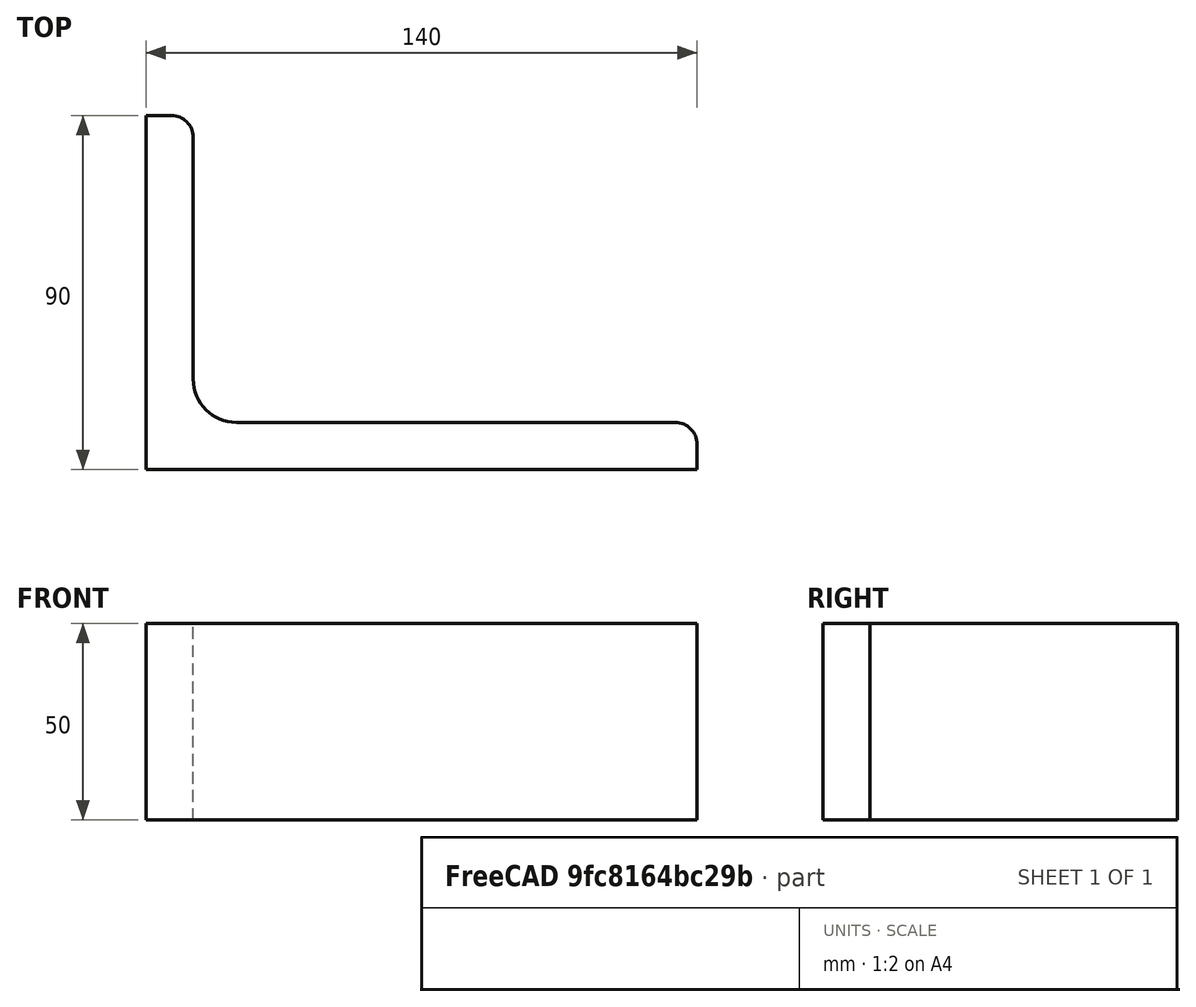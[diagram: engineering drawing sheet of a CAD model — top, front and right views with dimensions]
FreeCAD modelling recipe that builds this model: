
FCSTD DOCUMENT  (FreeCAD 0.15R4671 (Git))
Label: Angle Bar 140x90x12 EN10056 S235JR
License: All rights reserved
LicenseURL: http://en.wikipedia.org/wiki/All_rights_reserved
objects: Sketcher::SketchObject×1, Part::Extrusion×1
note: 2 computed .brp shape members not serialized (recipe doc carries the construction recipe); baked Part::Feature solids carry a one-line shape summary decoded from their .brp

FEATURE [Sketcher::SketchObject] Sketch
  sketch-geometry (9):
    g0: LineSegment StartX=0 StartY=0 StartZ=0 EndX=140 EndY=0 EndZ=0
    g1: LineSegment StartX=140 StartY=0 StartZ=0 EndX=140 EndY=6.5 EndZ=0
    g2: LineSegment StartX=134.5 StartY=12 StartZ=0 EndX=23 EndY=12 EndZ=0
    g3: LineSegment StartX=0 StartY=0 StartZ=0 EndX=0 EndY=90 EndZ=0
    g4: LineSegment StartX=0 StartY=90 StartZ=0 EndX=6.5 EndY=90 EndZ=0
    g5: LineSegment StartX=12 StartY=84.5 StartZ=0 EndX=12 EndY=23 EndZ=0
    g6: ArcOfCircle CenterX=23 CenterY=23 CenterZ=0 NormalX=0 NormalY=0 NormalZ=1 Radius=11 StartAngle=3.14159 EndAngle=4.71239
    g7: ArcOfCircle CenterX=6.5 CenterY=84.5 CenterZ=0 NormalX=0 NormalY=0 NormalZ=1 Radius=5.5 StartAngle=0 EndAngle=1.5708
    g8: ArcOfCircle CenterX=134.5 CenterY=6.5 CenterZ=0 NormalX=0 NormalY=0 NormalZ=1 Radius=5.5 StartAngle=0 EndAngle=1.5708
  constraints (23):
    c: Coincident(g0,g-1)
    c: Horizontal(g0)
    c: Coincident(g1,g0)
    c: Vertical(g1)
    c: Horizontal(g2)
    c: Coincident(g3,g-1)
    c: Vertical(g3)
    c: Coincident(g4,g3)
    c: Horizontal(g4)
    c: Vertical(g5)
    c: Tangent(g5,g6) = -1.5708
    c: Tangent(g2,g6) = 1.5708
    c: Tangent(g4,g7) = 1.5708
    c: Tangent(g5,g7) = 1.5708
    c: Tangent(g2,g8) = -1.5708
    c: Tangent(g1,g8) = -1.5708
    c: DistanceX(g0) = 140
    c: DistanceY(g3) = 90
    c: DistanceY(g0,g2) = 12
    c: DistanceX(g3,g5) = 12
    c: Radius(g6) = 11
    c: Radius(g8) = 5.5
    c: Radius(g7) = 5.5
FEATURE [Part::Extrusion] Extrude  label="Angle Bar 140x90x12 EN10056 S235JR"
  Base = -> Sketch
  Dir = (0,0,50)
  Solid = true
